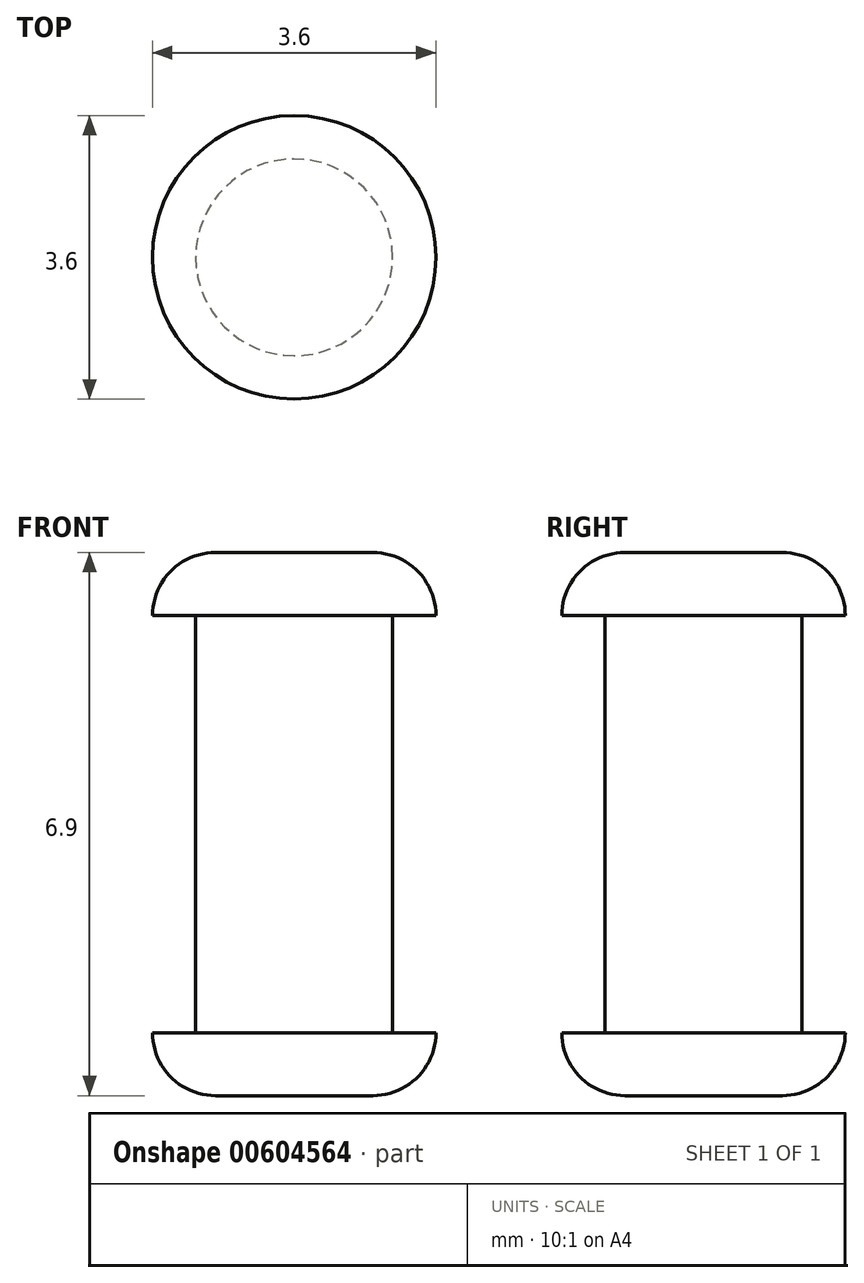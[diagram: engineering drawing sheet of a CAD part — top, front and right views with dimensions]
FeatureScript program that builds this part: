
annotation { "Feature Type Name" : "Feature", "Feature Type Description" : "" }
export const myFeature = defineFeature(function(context is Context, id is Id, definition is map)
    precondition{}
    {
        {
            var Q0;
            Q0=qCreatedBy(makeId("Front.planeOp"),FACE);
            var sketch = newSketch(context, id + "F0", { "sketchPlane" : qUnion([Q0])});
            skLineSegment(sketch, "E0.left", {"start": v(-1.25, 2.65) * mm, "end": v(-1.25, -2.65) * mm});
            skLineSegment(sketch, "E1", {"start": v(-1.25, 2.65) * mm, "end": v(-1.8, 2.65) * mm});
            skLineSegment(sketch, "E2", {"start": v(-1.8, 2.65) * mm, "end": v(-1.8, 3.45) * mm});
            skLineSegment(sketch, "E3", {"start": v(-1.8, 3.45) * mm, "end": v(0, 3.45) * mm});
            skLineSegment(sketch, "E4", {"start": v(0, 3.45) * mm, "end": v(0, 0) * mm});
            skLineSegment(sketch, "E5", {"start": v(0, 0) * mm, "end": v(0, -3.45) * mm});
            skLineSegment(sketch, "E6", {"start": v(0, -3.45) * mm, "end": v(-1.8, -3.45) * mm});
            skLineSegment(sketch, "E7", {"start": v(-1.8, -3.45) * mm, "end": v(-1.8, -2.65) * mm});
            skLineSegment(sketch, "E8", {"start": v(-1.8, -2.65) * mm, "end": v(-1.25, -2.65) * mm});
            skLineSegment(sketch, "E9", {"start": v(0, 8.16) * mm, "end": v(0, -9.3) * mm, "construction": true});
            skSolve(sketch);
        }
        {
            var Q0;
            Q0=makeQuery(id+"F0.imprint","IMPRINT",FACE,{"disambiguationData":[TD([[makeQuery(id+"F0.imprint","IMPRINT",EDGE,{"derivedFrom":sQuery(id+"F0.wireOp",EDGE,"E0.left")}),1.0]])]});
            var Q1;
            Q1=sQuery(id+"F0.wireOp",EDGE,"E9");
            revolve(context, id + "F1", {"entities" : qUnion([Q0]), "axis" : qUnion([Q1]), "revolveType" : RevolveType.FULL});
        }
        {
            var Q0;
            Q0=makeQuery(id+"F1.opRevolve","SWEPT_EDGE",EDGE,{"disambiguationData":[OSD([sQuery(id+"F0.wireOp",EDGE,"E2"),sQuery(id+"F0.wireOp",EDGE,"E3")])]});
            var Q1;
            Q1=makeQuery(id+"F1.opRevolve","SWEPT_EDGE",EDGE,{"disambiguationData":[OSD([sQuery(id+"F0.wireOp",EDGE,"E6"),sQuery(id+"F0.wireOp",EDGE,"E7")])]});
            fillet(context, id + "F2", {"entities" : qUnion([Q0, Q1]), "radius" : 0.8 * mm, "tangentPropagation" : true, "allowEdgeOverflow" : false});
        }
    });
